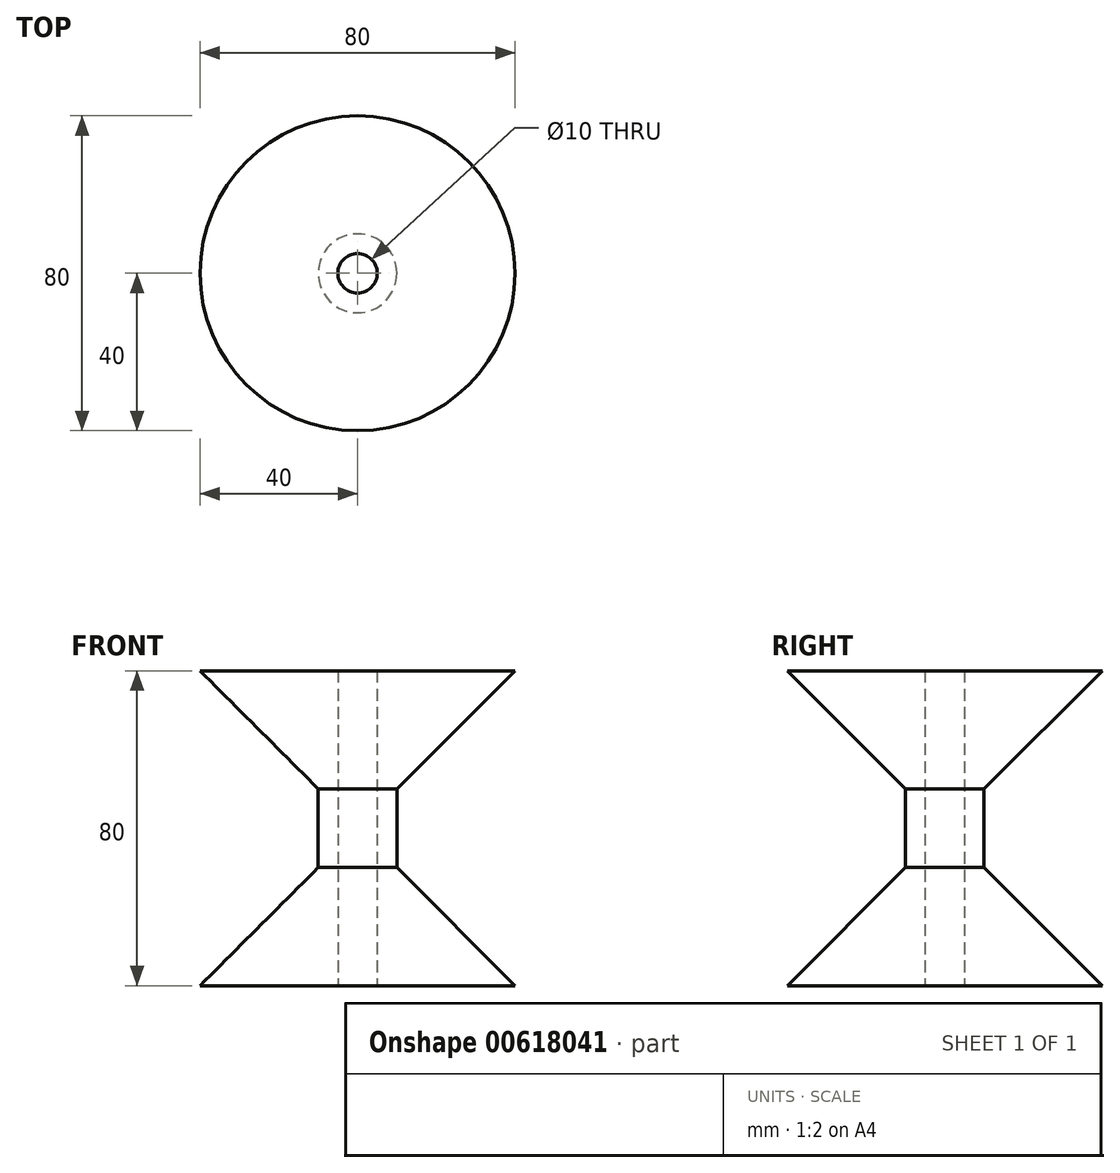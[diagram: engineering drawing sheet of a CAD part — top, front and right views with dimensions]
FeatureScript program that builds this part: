
annotation { "Feature Type Name" : "Feature", "Feature Type Description" : "" }
export const myFeature = defineFeature(function(context is Context, id is Id, definition is map)
    precondition{}
    {
        {
            var Q0;
            Q0=qCreatedBy(makeId("Front.planeOp"),FACE);
            var sketch = newSketch(context, id + "F0", { "sketchPlane" : qUnion([Q0])});
            skLineSegment(sketch, "E0", {"start": v(0, 0) * mm, "end": v(0, 80) * mm});
            skLineSegment(sketch, "E1", {"start": v(0, 80) * mm, "end": v(-40, 80) * mm});
            skLineSegment(sketch, "E2", {"start": v(-40, 80) * mm, "end": v(-10, 50) * mm});
            skLineSegment(sketch, "E3", {"start": v(-10, 50) * mm, "end": v(-10, 30) * mm});
            skLineSegment(sketch, "E4", {"start": v(-10, 30) * mm, "end": v(-40, 0) * mm});
            skLineSegment(sketch, "E5", {"start": v(-40, 0) * mm, "end": v(0, 0) * mm});
            skSolve(sketch);
        }
        {
            var Q0;
            Q0 = qSketchRegion(id + "F0", true);
            var Q1;
            Q1=sQuery(id+"F0.wireOp",EDGE,"E0");
            revolve(context, id + "F1", {"entities" : qUnion([Q0]), "axis" : qUnion([Q1]), "revolveType" : RevolveType.FULL});
        }
        {
            var Q0;
            Q0=makeQuery(id+"F1.opRevolve","SWEPT_FACE",FACE,{"disambiguationData":[OSD([sQuery(id+"F0.wireOp",EDGE,"E5")])]});
            var sketch = newSketch(context, id + "F2", { "sketchPlane" : qUnion([Q0])});
            skCircle(sketch, "E6", {"center": v(0, 0) * mm, "radius": 5 * mm});
            skSolve(sketch);
        }
        {
            var Q0;
            Q0 = qSketchRegion(id + "F2", true);
            extrude(context, id + "F3", {"entities" : qUnion([Q0]), "operationType" : NewBodyOperationType.REMOVE, "endBound" : BoundingType.UP_TO_NEXT, "oppositeDirection" : true, "depth" : 25 * mm, "offsetDistance" : 25 * mm});
        }
    });
